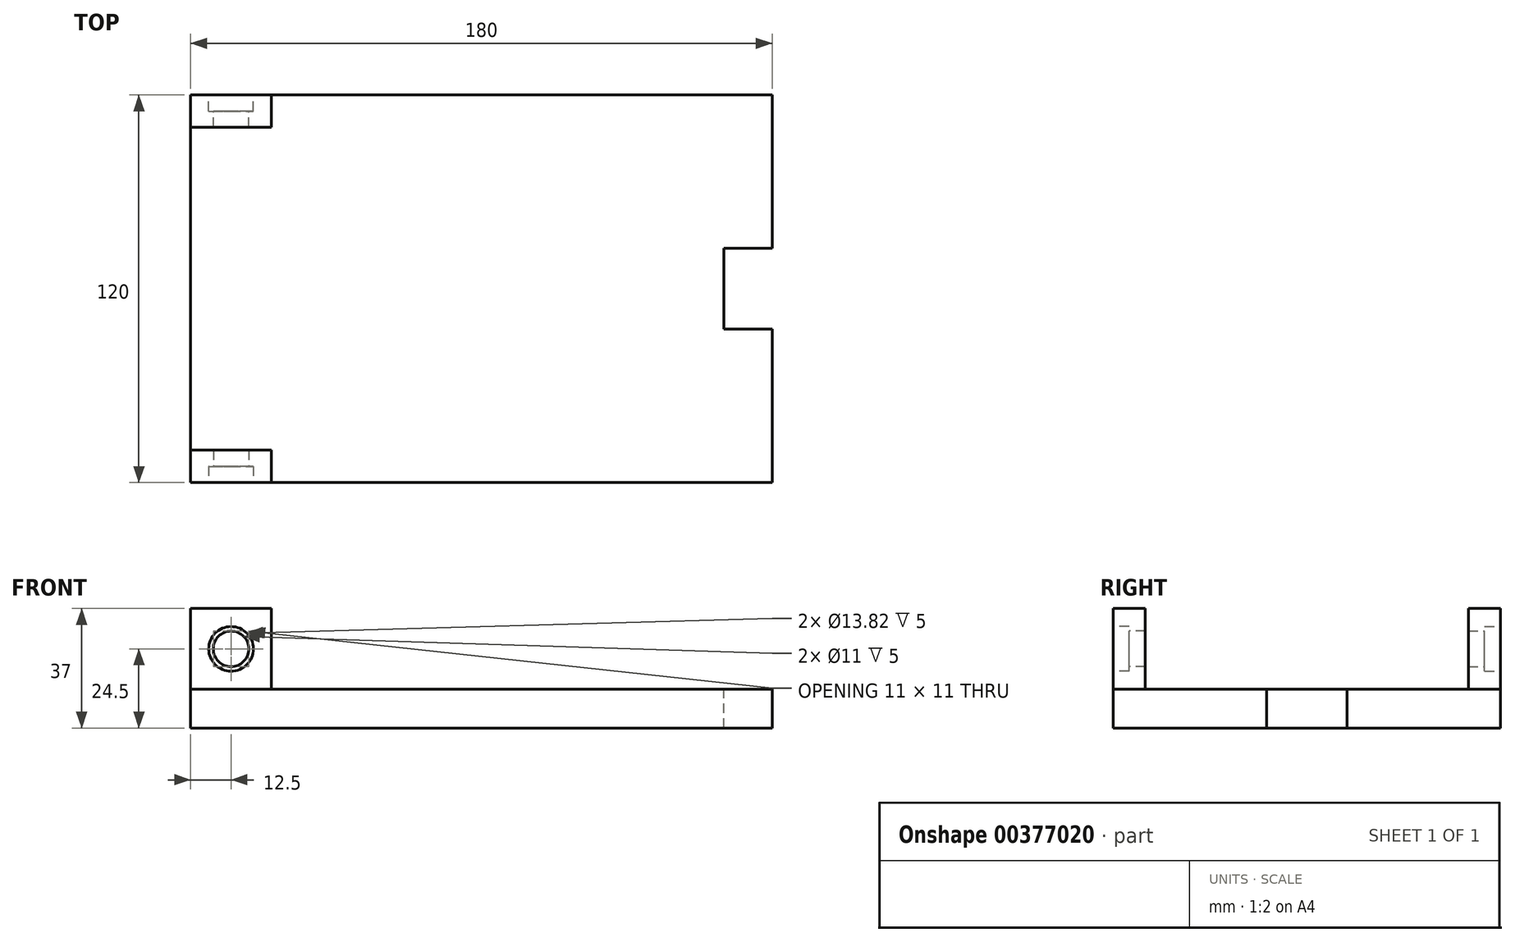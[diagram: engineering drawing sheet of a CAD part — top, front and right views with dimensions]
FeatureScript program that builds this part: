
annotation { "Feature Type Name" : "Feature", "Feature Type Description" : "" }
export const myFeature = defineFeature(function(context is Context, id is Id, definition is map)
    precondition{}
    {
        {
            var Q0;
            Q0=qCreatedBy(makeId("Top.planeOp"),FACE);
            var sketch = newSketch(context, id + "F0", { "sketchPlane" : qUnion([Q0])});
            skLineSegment(sketch, "E0.bottom", {"start": v(-90, 60) * mm, "end": v(90, 60) * mm});
            skLineSegment(sketch, "E0.top", {"start": v(-90, -60) * mm, "end": v(90, -60) * mm});
            skLineSegment(sketch, "E0.left", {"start": v(-90, 60) * mm, "end": v(-90, -60) * mm});
            skLineSegment(sketch, "E0.right", {"start": v(90, 60) * mm, "end": v(90, -60) * mm});
            skSolve(sketch);
        }
        {
            var Q0;
            Q0 = qSketchRegion(id + "F0", true);
            extrude(context, id + "F1", {"entities" : qUnion([Q0]), "depth" : 12 * mm});
        }
        {
            var Q0;
            Q0=makeQuery(id+"F1.opExtrude","CAP_FACE",FACE,{"disambiguationData":[OSD([sQuery(id+"F0.wireOp",EDGE,"E0.bottom"),sQuery(id+"F0.wireOp",EDGE,"E0.top"),sQuery(id+"F0.wireOp",EDGE,"E0.left"),sQuery(id+"F0.wireOp",EDGE,"E0.right")])],"isStart":false});
            var sketch = newSketch(context, id + "F2", { "sketchPlane" : qUnion([Q0])});
            skLineSegment(sketch, "E1.bottom", {"start": v(-90, -60) * mm, "end": v(-65, -60) * mm});
            skLineSegment(sketch, "E1.top", {"start": v(-90, -50) * mm, "end": v(-65, -50) * mm});
            skLineSegment(sketch, "E1.left", {"start": v(-90, -60) * mm, "end": v(-90, -50) * mm});
            skLineSegment(sketch, "E1.right", {"start": v(-65, -60) * mm, "end": v(-65, -50) * mm});
            skSolve(sketch);
        }
        {
            var Q0;
            Q0 = qSketchRegion(id + "F2", true);
            extrude(context, id + "F3", {"entities" : qUnion([Q0]), "depth" : 25 * mm});
        }
        {
            var Q0;
            Q0=makeQuery(id+"F3.opExtrude","SWEPT_FACE",FACE,{"disambiguationData":[OSD([sQuery(id+"F2.wireOp",EDGE,"E1.bottom")])]});
            var sketch = newSketch(context, id + "F4", { "sketchPlane" : qUnion([Q0])});
            skCircle(sketch, "E2", {"center": v(-77.5, 24.5) * mm, "radius": 6.91 * mm});
            skSolve(sketch);
        }
        {
            var Q0;
            Q0 = qSketchRegion(id + "F4", true);
            extrude(context, id + "F5", {"entities" : qUnion([Q0]), "operationType" : NewBodyOperationType.REMOVE, "oppositeDirection" : true, "depth" : 5 * mm});
        }
        {
            var Q0;
            Q0=makeQuery(id+"F5.boolean.opBoolean","COPY",FACE,{"derivedFrom":makeQuery(id+"F5.opExtrude","CAP_FACE",FACE,{"disambiguationData":[OSD([sQuery(id+"F4.wireOp",EDGE,"E2")])],"isStart":false})});
            var sketch = newSketch(context, id + "F6", { "sketchPlane" : qUnion([Q0])});
            skCircle(sketch, "E3", {"center": v(-77.5, 24.5) * mm, "radius": 5.5 * mm});
            skSolve(sketch);
        }
        {
            var Q0;
            Q0 = qSketchRegion(id + "F6", true);
            extrude(context, id + "F7", {"entities" : qUnion([Q0]), "operationType" : NewBodyOperationType.REMOVE, "oppositeDirection" : true, "depth" : 200 * mm});
        }
        {
            var Q0;
            Q0=makeQuery(id+"F3.opExtrude","SWEPT_BODY",BODY,{"disambiguationData":[OSD([sQuery(id+"F2.wireOp",EDGE,"E1.bottom"),sQuery(id+"F2.wireOp",EDGE,"E1.top"),sQuery(id+"F2.wireOp",EDGE,"E1.left"),sQuery(id+"F2.wireOp",EDGE,"E1.right")])]});
            var Q1;
            Q1=qCreatedBy(makeId("Front.planeOp"),FACE);
            mirror(context, id + "F8", {"entities" : qUnion([Q0]), "mirrorPlane" : qUnion([Q1])});
        }
        {
            var Q0;
            Q0=makeQuery(id+"F1.opExtrude","CAP_FACE",FACE,{"disambiguationData":[OSD([sQuery(id+"F0.wireOp",EDGE,"E0.bottom"),sQuery(id+"F0.wireOp",EDGE,"E0.top"),sQuery(id+"F0.wireOp",EDGE,"E0.left"),sQuery(id+"F0.wireOp",EDGE,"E0.right")])],"isStart":false});
            var sketch = newSketch(context, id + "F9", { "sketchPlane" : qUnion([Q0])});
            skLineSegment(sketch, "E4.bottom", {"start": v(90, 12.5) * mm, "end": v(75, 12.5) * mm});
            skLineSegment(sketch, "E4.top", {"start": v(90, -12.5) * mm, "end": v(75, -12.5) * mm});
            skLineSegment(sketch, "E4.left", {"start": v(90, 12.5) * mm, "end": v(90, -12.5) * mm});
            skLineSegment(sketch, "E4.right", {"start": v(75, 12.5) * mm, "end": v(75, -12.5) * mm});
            skSolve(sketch);
        }
        {
            var Q0;
            Q0 = qSketchRegion(id + "F9", true);
            extrude(context, id + "F10", {"entities" : qUnion([Q0]), "operationType" : NewBodyOperationType.REMOVE, "oppositeDirection" : true, "depth" : 25 * mm});
        }
    });
